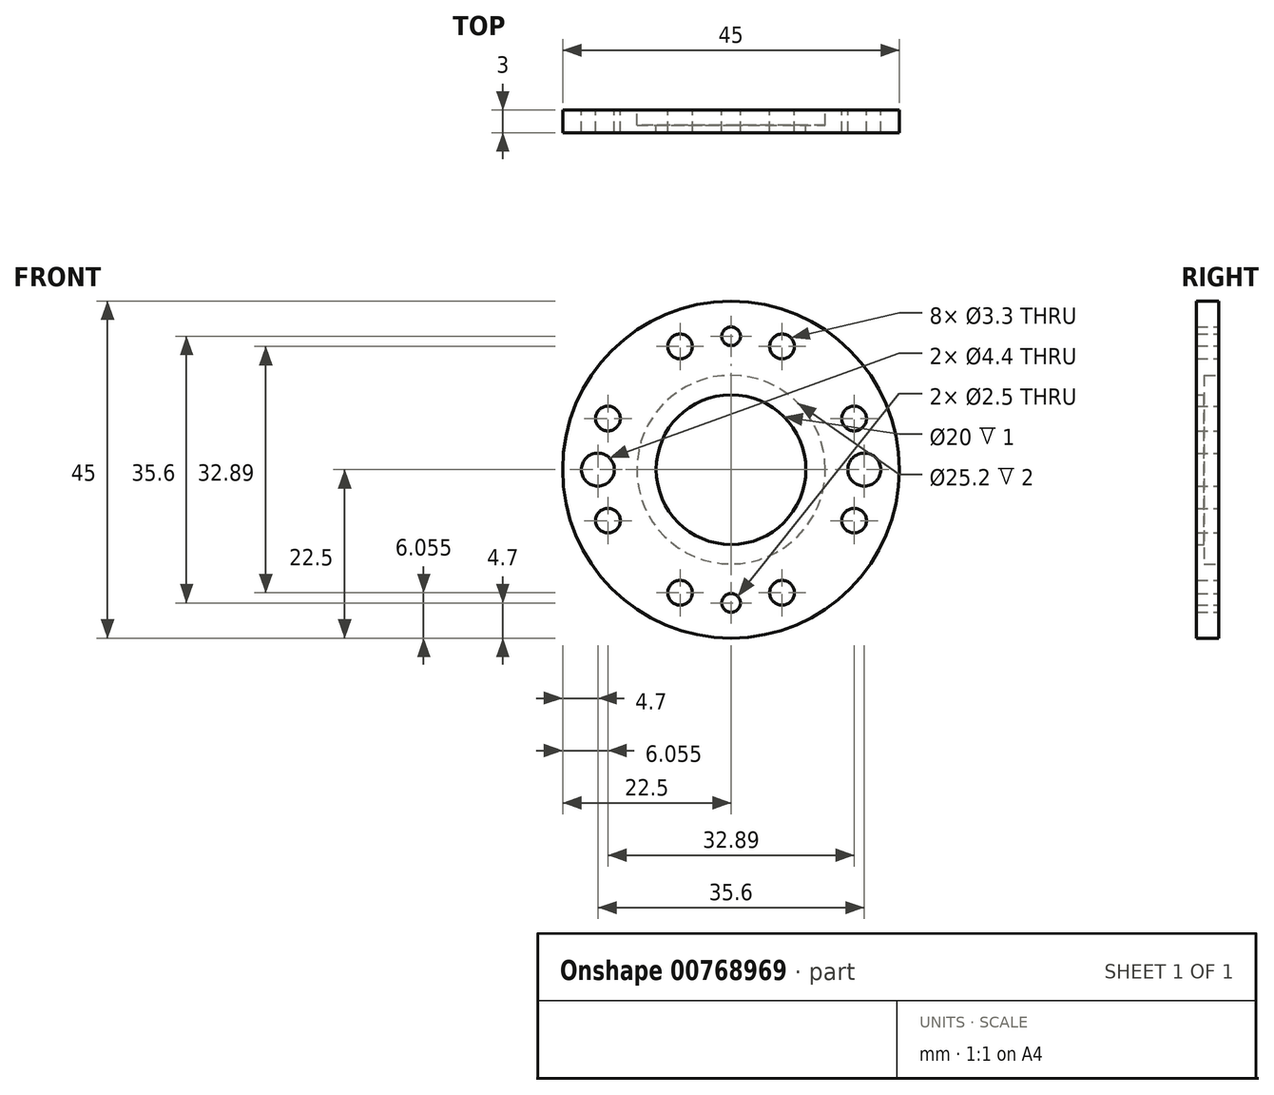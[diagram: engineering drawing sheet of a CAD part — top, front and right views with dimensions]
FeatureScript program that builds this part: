
annotation { "Feature Type Name" : "Feature", "Feature Type Description" : "" }
export const myFeature = defineFeature(function(context is Context, id is Id, definition is map)
    precondition{}
    {
        {
            var Q0;
            Q0=qCreatedBy(makeId("Front.planeOp"),FACE);
            var sketch = newSketch(context, id + "F0", { "sketchPlane" : qUnion([Q0])});
            skCircle(sketch, "E0", {"center": v(0, 0) * mm, "radius": 22.5 * mm});
            skCircle(sketch, "E1", {"center": v(0, 0) * mm, "radius": 10 * mm});
            skCircle(sketch, "E2", {"center": v(0, 0) * mm, "radius": 17.8 * mm, "construction": true});
            skLineSegment(sketch, "E3", {"start": v(0, 0) * mm, "end": v(-32.16, 13.32) * mm, "construction": true});
            skPoint(sketch, "E4", {"position": v(-16.45, 6.81) * mm});
            skPoint(sketch, "E5.1.0", {"position": v(-16.45, -6.81) * mm});
            skPoint(sketch, "E5.2.0", {"position": v(-6.81, -16.45) * mm});
            skPoint(sketch, "E5.3.0", {"position": v(6.81, -16.45) * mm});
            skPoint(sketch, "E5.4.0", {"position": v(16.45, -6.81) * mm});
            skPoint(sketch, "E5.5.0", {"position": v(16.45, 6.81) * mm});
            skPoint(sketch, "E5.6.0", {"position": v(6.81, 16.45) * mm});
            skPoint(sketch, "E5.7.0", {"position": v(-6.81, 16.45) * mm});
            skPoint(sketch, "E6", {"position": v(-17.8, 0) * mm});
            skPoint(sketch, "E7", {"position": v(17.8, 0) * mm});
            skPoint(sketch, "E8", {"position": v(0, 17.8) * mm});
            skPoint(sketch, "E9", {"position": v(0, -17.8) * mm});
            skSolve(sketch);
        }
        {
            var Q0;
            Q0=makeQuery(id+"F0.imprint","IMPRINT",FACE,{"disambiguationData":[TD([[makeQuery(id+"F0.imprint","IMPRINT",EDGE,{"derivedFrom":sQuery(id+"F0.wireOp",EDGE,"E0")}),1.0]])]});
            extrude(context, id + "F1", {"entities" : qUnion([Q0]), "depth" : 3 * mm, "offsetDistance" : 25 * mm});
        }
        {
            var Q0;
            Q0=sQuery(id+"F0.wireOp",VERTEX,"E4");
            var Q1;
            Q1=sQuery(id+"F0.wireOp",VERTEX,"E5.7.0");
            var Q2;
            Q2=sQuery(id+"F0.wireOp",VERTEX,"E5.6.0");
            var Q3;
            Q3=sQuery(id+"F0.wireOp",VERTEX,"E5.5.0");
            var Q4;
            Q4=sQuery(id+"F0.wireOp",VERTEX,"E5.4.0");
            var Q5;
            Q5=sQuery(id+"F0.wireOp",VERTEX,"E5.3.0");
            var Q6;
            Q6=sQuery(id+"F0.wireOp",VERTEX,"E5.2.0");
            var Q7;
            Q7=sQuery(id+"F0.wireOp",VERTEX,"E5.1.0");
            var Q8;
            Q8=makeQuery(id+"F1.opExtrude","SWEPT_BODY",BODY,{"disambiguationData":[OSD([sQuery(id+"F0.wireOp",EDGE,"E0"),sQuery(id+"F0.wireOp",EDGE,"E1")])]});
            hole(context, id + "F2", {"style" : HoleStyle.SIMPLE, "endStyle" : HoleEndStyle.THROUGH, "oppositeDirection" : true, "standardTappedOrClearance" : lookupTablePath({ "standard" : "ISO", "fit" : "Normal", "size" : "M3", "type" : "Clearance" }), "standardBlindInLast" : lookupTablePath({ "fit" : "Standard", "standard" : "ISO", "size" : "M3", "type" : "Clearance" }), "holeDiameter" : 3.3 * mm, "majorDiameter" : 5 * mm, "isTappedThrough" : true, "tappedDepth" : 12 * mm, "tapClearance" : 3, "locations" : qUnion([Q0, Q1, Q2, Q3, Q4, Q5, Q6, Q7]), "scope" : qUnion([Q8])});
        }
        {
            var Q0;
            Q0=sQuery(id+"F0.wireOp",VERTEX,"E6");
            var Q1;
            Q1=sQuery(id+"F0.wireOp",VERTEX,"E7");
            var Q2;
            Q2=makeQuery(id+"F1.opExtrude","SWEPT_BODY",BODY,{"disambiguationData":[OSD([sQuery(id+"F0.wireOp",EDGE,"E0"),sQuery(id+"F0.wireOp",EDGE,"E1")])]});
            hole(context, id + "F3", {"style" : HoleStyle.SIMPLE, "endStyle" : HoleEndStyle.THROUGH, "oppositeDirection" : true, "standardTappedOrClearance" : lookupTablePath({ "standard" : "ISO", "fit" : "Normal", "size" : "M4", "type" : "Clearance" }), "standardBlindInLast" : lookupTablePath({ "fit" : "Standard", "standard" : "ISO", "size" : "M4", "type" : "Clearance" }), "holeDiameter" : 4.4 * mm, "majorDiameter" : 3 * mm, "isTappedThrough" : true, "tappedDepth" : 12 * mm, "tapClearance" : 3, "locations" : qUnion([Q0, Q1]), "scope" : qUnion([Q2])});
        }
        {
            var Q0;
            Q0=makeQuery(id+"F1.opExtrude","CAP_FACE",FACE,{"disambiguationData":[OSD([sQuery(id+"F0.wireOp",EDGE,"E0"),sQuery(id+"F0.wireOp",EDGE,"E1")])],"isStart":true});
            var sketch = newSketch(context, id + "F4", { "sketchPlane" : qUnion([Q0])});
            skCircle(sketch, "E10", {"center": v(0, 0) * mm, "radius": 12.6 * mm});
            skSolve(sketch);
        }
        {
            var Q0;
            Q0=makeQuery(id+"F4.imprint","IMPRINT",FACE,{"disambiguationData":[TD([[makeQuery(id+"F4.imprint","IMPRINT",EDGE,{"derivedFrom":sQuery(id+"F4.wireOp",EDGE,"E10")}),1.0]])]});
            extrude(context, id + "F5", {"entities" : qUnion([Q0]), "operationType" : NewBodyOperationType.REMOVE, "oppositeDirection" : true, "depth" : 2 * mm, "offsetDistance" : 25 * mm});
        }
        {
            var Q0;
            Q0=sQuery(id+"F0.wireOp",VERTEX,"E8");
            var Q1;
            Q1=sQuery(id+"F0.wireOp",VERTEX,"E9");
            var Q2;
            Q2=makeQuery(id+"F1.opExtrude","SWEPT_BODY",BODY,{"disambiguationData":[OSD([sQuery(id+"F0.wireOp",EDGE,"E0"),sQuery(id+"F0.wireOp",EDGE,"E1")])]});
            hole(context, id + "F6", {"style" : HoleStyle.SIMPLE, "endStyle" : HoleEndStyle.THROUGH, "oppositeDirection" : true, "standardTappedOrClearance" : lookupTablePath({ "standard" : "ISO", "engagement" : "75%", "pitch" : "0.5 mm", "size" : "M3", "type" : "Tapped" }), "standardBlindInLast" : lookupTablePath({ "standard" : "ISO", "engagement" : "75%", "pitch" : "0.5 mm", "size" : "M3", "type" : "Tapped" }), "holeDiameter" : 2.5 * mm, "majorDiameter" : 3 * mm, "showTappedDepth" : true, "isTappedThrough" : true, "tappedDepth" : 12 * mm, "tapClearance" : 3, "locations" : qUnion([Q0, Q1]), "scope" : qUnion([Q2])});
        }
    });
